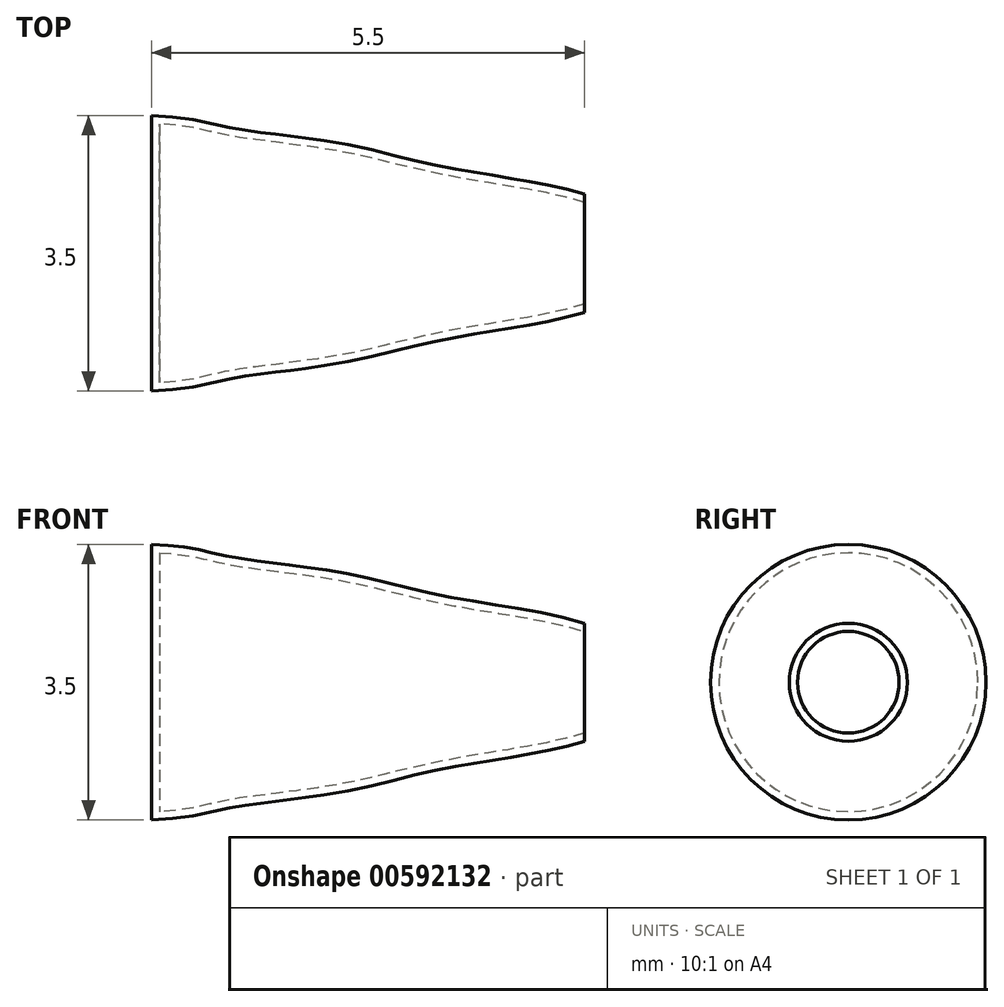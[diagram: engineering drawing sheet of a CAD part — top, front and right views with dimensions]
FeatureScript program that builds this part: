
annotation { "Feature Type Name" : "Feature", "Feature Type Description" : "" }
export const myFeature = defineFeature(function(context is Context, id is Id, definition is map)
    precondition{}
    {
        {
            var Q0;
            Q0=qCreatedBy(makeId("Top.planeOp"),FACE);
            var sketch = newSketch(context, id + "F0", { "sketchPlane" : qUnion([Q0])});
            skLineSegment(sketch, "E0", {"start": v(0, 0) * mm, "end": v(11, 0) * mm});
            skLineSegment(sketch, "E1", {"start": v(0, 0) * mm, "end": v(0, 3.5) * mm});
            skLineSegment(sketch, "E2", {"start": v(11, 0) * mm, "end": v(11, 1.5) * mm});
            skFitSpline(sketch, "E3", {"points": [v(0, 3.5) * mm, v(1, 3.4) * mm, v(1.77, 3.23) * mm, v(2.7, 3.08) * mm, v(3.77, 2.95) * mm, v(5.34, 2.68) * mm, v(7.07, 2.27) * mm, v(9.01, 1.92) * mm, v(11, 1.5) * mm], "startDerivative": vector(9.7, -0.55) * mm, "endDerivative": vector(12.06, -3.59) * mm});
            skSolve(sketch);
        }
        {
            var Q0;
            Q0=makeQuery(id+"F0.imprint","IMPRINT",FACE,{"disambiguationData":[TD([[makeQuery(id+"F0.imprint","IMPRINT",EDGE,{"derivedFrom":sQuery(id+"F0.wireOp",EDGE,"E0")}),1.0]])]});
            var Q1;
            Q1=sQuery(id+"F0.wireOp",EDGE,"E0");
            revolve(context, id + "F1", {"entities" : qUnion([Q0]), "axis" : qUnion([Q1]), "revolveType" : RevolveType.FULL});
        }
        {
            var Q0;
            Q0=makeQuery(id+"F1.opRevolve","SWEPT_BODY",BODY,{"disambiguationData":[OSD([sQuery(id+"F0.wireOp",EDGE,"E0"),sQuery(id+"F0.wireOp",EDGE,"E1"),sQuery(id+"F0.wireOp",EDGE,"E2"),sQuery(id+"F0.wireOp",EDGE,"E3")])]});
            var Q1;
            Q1=qCreatedBy(makeId("Origin.pointOp"),VERTEX);
            transform(context, id + "F2", {"entities" : qUnion([Q0]), "transformType" : TransformType.SCALE_UNIFORMLY, "scale" : .5, "scalePoint" : qUnion([Q1]), "makeCopy" : false});
        }
        {
            var Q0;
            Q0=makeQuery(id+"F1.opRevolve","SWEPT_FACE",FACE,{"disambiguationData":[OSD([sQuery(id+"F0.wireOp",EDGE,"E2")])]});
            shell(context, id + "F3", {"entities" : qUnion([Q0]), "thickness" : 0.1 * mm});
        }
    });
